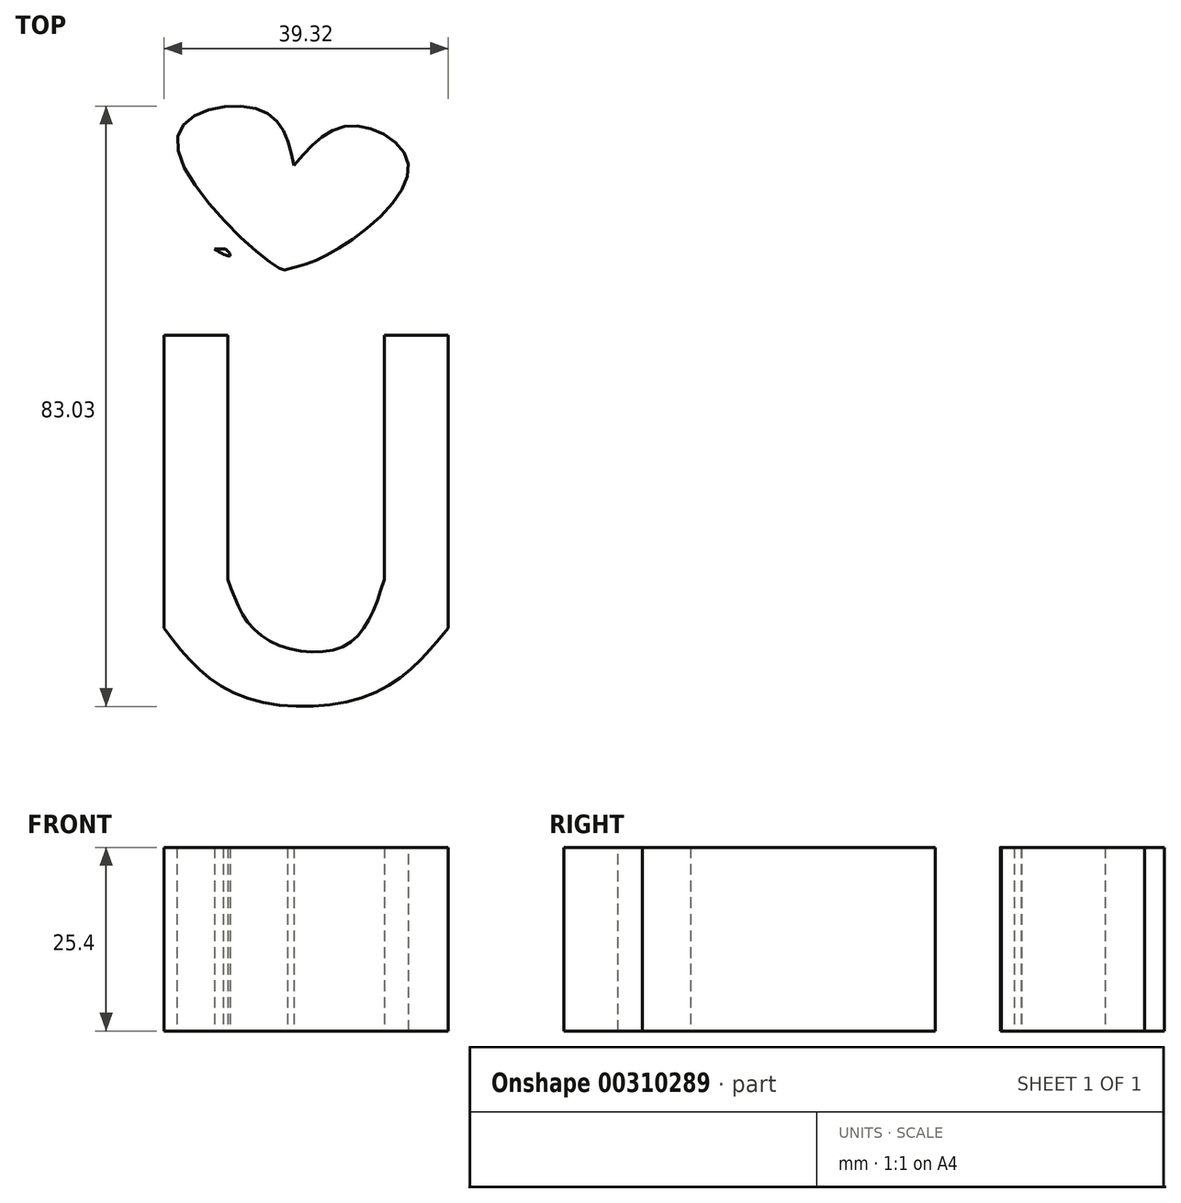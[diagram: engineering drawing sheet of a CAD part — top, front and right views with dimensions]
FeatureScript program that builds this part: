
annotation { "Feature Type Name" : "Feature", "Feature Type Description" : "" }
export const myFeature = defineFeature(function(context is Context, id is Id, definition is map)
    precondition{}
    {
        {
            var Q0;
            Q0=qCreatedBy(makeId("Top.planeOp"),FACE);
            var sketch = newSketch(context, id + "F0", { "sketchPlane" : qUnion([Q0])});
            skFitSpline(sketch, "E0", {"points": [v(-19.5, 33.99) * mm, v(-27.13, 41.6) * mm, v(-39.01, 42.52) * mm, v(-46.02, 29.41) * mm, v(-30.18, 14.48) * mm, v(-30.78, 15.4) * mm, v(-31.09, 15.4) * mm], "startDerivative": vector(-34.36, 44.55) * mm, "endDerivative": vector(-7.54, -3.8) * mm});
            skFitSpline(sketch, "E1", {"points": [v(-19.5, 33.99) * mm, v(-11.58, 38.56) * mm, v(0, 43.13) * mm, v(10.67, 37.34) * mm, v(0, 19.96) * mm, v(-8.53, 14.78) * mm, v(-8.23, 14.17) * mm], "startDerivative": vector(46.7, 26.19) * mm, "endDerivative": vector(12.72, -13.04) * mm});
            skFitSpline(sketch, "E2", {"points": [v(-30.78, 15.4) * mm, v(-50.9, 15.4) * mm, v(-51.82, 15.4) * mm], "startDerivative": vector(-32.32, 0) * mm, "endDerivative": vector(-3.52, 0) * mm});
            skFitSpline(sketch, "E3", {"points": [v(-51.61, 15.4) * mm, v(-50.9, -53.5) * mm, v(-50.9, -52.88) * mm], "startDerivative": vector(1.13, -113.05) * mm, "endDerivative": vector(-0.03, 10.63) * mm});
            skFitSpline(sketch, "E4", {"points": [v(-8.23, 14.17) * mm, v(11.89, 14.17) * mm], "startDerivative": vector(20.12, 0) * mm, "endDerivative": vector(20.12, 0) * mm});
            skFitSpline(sketch, "E5", {"points": [v(11.89, 14.17) * mm, v(11.89, -53.19) * mm], "startDerivative": vector(0, -67.36) * mm, "endDerivative": vector(0, -67.36) * mm});
            skFitSpline(sketch, "E6", {"points": [v(-50.9, -53.19) * mm, v(11.89, -53.19) * mm], "startDerivative": vector(62.79, 0) * mm, "endDerivative": vector(62.79, 0) * mm});
            skLineSegment(sketch, "E7", {"start": v(-39.32, 3.5) * mm, "end": v(-30.48, 3.5) * mm});
            skLineSegment(sketch, "E8", {"start": v(-8.84, 3.5) * mm, "end": v(0, 3.5) * mm});
            skLineSegment(sketch, "E9", {"start": v(-39.32, 3.5) * mm, "end": v(-39.32, -37.03) * mm});
            skLineSegment(sketch, "E10", {"start": v(0, 3.5) * mm, "end": v(0, -37.03) * mm});
            skFitSpline(sketch, "E11", {"points": [v(-39.32, -37.03) * mm, v(-29.26, -46.18) * mm, v(-10.67, -46.18) * mm, v(0, -37.03) * mm], "startDerivative": vector(26.28, -34.47) * mm, "endDerivative": vector(27.86, 33.87) * mm});
            skLineSegment(sketch, "E12", {"start": v(-30.48, 3.5) * mm, "end": v(-30.48, -30.33) * mm});
            skLineSegment(sketch, "E13", {"start": v(-8.84, 3.5) * mm, "end": v(-8.84, -30.33) * mm});
            skFitSpline(sketch, "E14", {"points": [v(-30.48, -30.33) * mm, v(-25.6, -38.25) * mm, v(-14.33, -39.47) * mm, v(-8.84, -30.33) * mm], "startDerivative": vector(10.12, -28.7) * mm, "endDerivative": vector(10.84, 33.7) * mm});
            skFitSpline(sketch, "E15", {"points": [v(-21.34, 26.97) * mm, v(-25.9, 34.6) * mm, v(-37.5, 30.63) * mm, v(-23.16, 12.65) * mm, v(-22.25, 12.65) * mm], "startDerivative": vector(-8.26, 39.34) * mm, "endDerivative": vector(6.9, 4.95) * mm});
            skFitSpline(sketch, "E16", {"points": [v(-21.34, 26.97) * mm, v(-13.41, 32.46) * mm, v(-5.49, 26.97) * mm, v(-15.24, 15.43) * mm, v(-22.25, 12.65) * mm], "startDerivative": vector(28.61, 33.3) * mm, "endDerivative": vector(-28.57, -7.06) * mm});
            skSolve(sketch);
        }
        {
            var Q0;
            Q0 = qSketchRegion(id + "F0", true);
            extrude(context, id + "F1", {"entities" : qUnion([Q0]), "depth" : 25.4 * mm});
        }
    });
